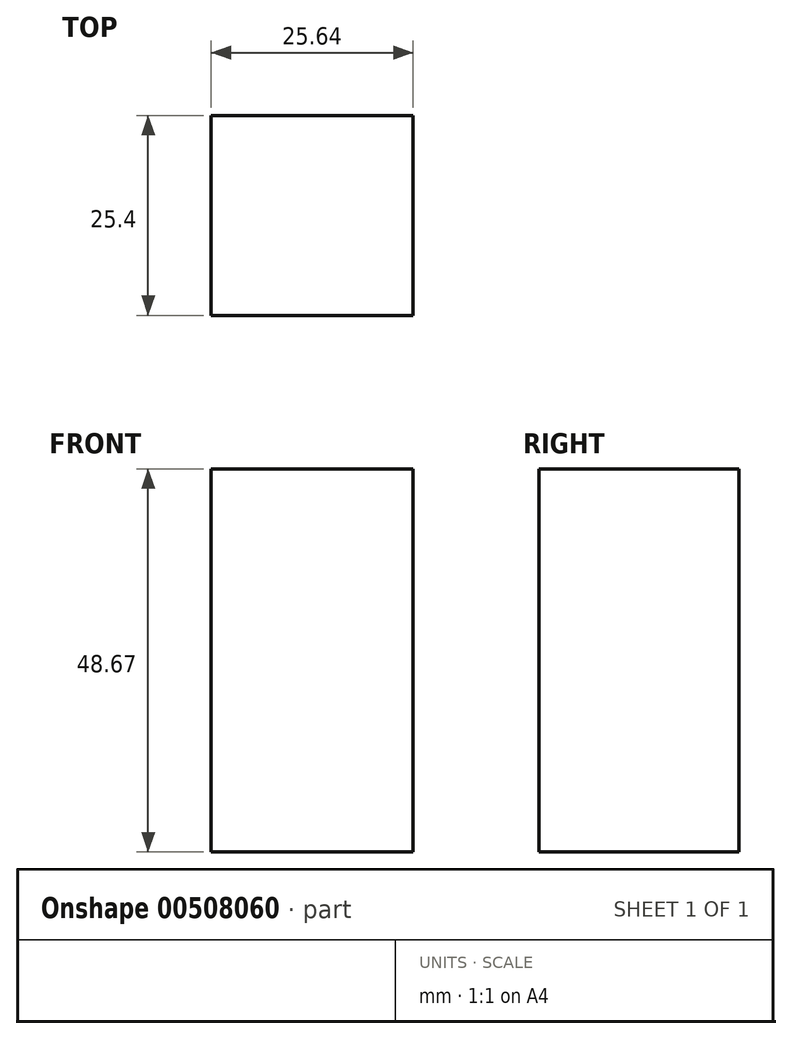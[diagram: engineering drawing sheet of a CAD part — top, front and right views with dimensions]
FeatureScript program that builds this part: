
annotation { "Feature Type Name" : "Feature", "Feature Type Description" : "" }
export const myFeature = defineFeature(function(context is Context, id is Id, definition is map)
    precondition{}
    {
        {
            var Q0;
            Q0=qCreatedBy(makeId("Front.planeOp"),FACE);
            var sketch = newSketch(context, id + "F0", { "sketchPlane" : qUnion([Q0])});
            skLineSegment(sketch, "E0.bottom", {"start": v(12.82, 23.46) * mm, "end": v(-12.82, 23.46) * mm});
            skLineSegment(sketch, "E0.top", {"start": v(12.82, -25.21) * mm, "end": v(-12.82, -25.21) * mm});
            skLineSegment(sketch, "E0.left", {"start": v(12.82, 23.46) * mm, "end": v(12.82, -25.21) * mm});
            skLineSegment(sketch, "E0.right", {"start": v(-12.82, 23.46) * mm, "end": v(-12.82, -25.21) * mm});
            skSolve(sketch);
        }
        {
            var Q0;
            Q0 = qSketchRegion(id + "F0", true);
            extrude(context, id + "F1", {"entities" : qUnion([Q0]), "endBound" : BoundingType.SYMMETRIC, "depth" : 25.4 * mm});
        }
    });
